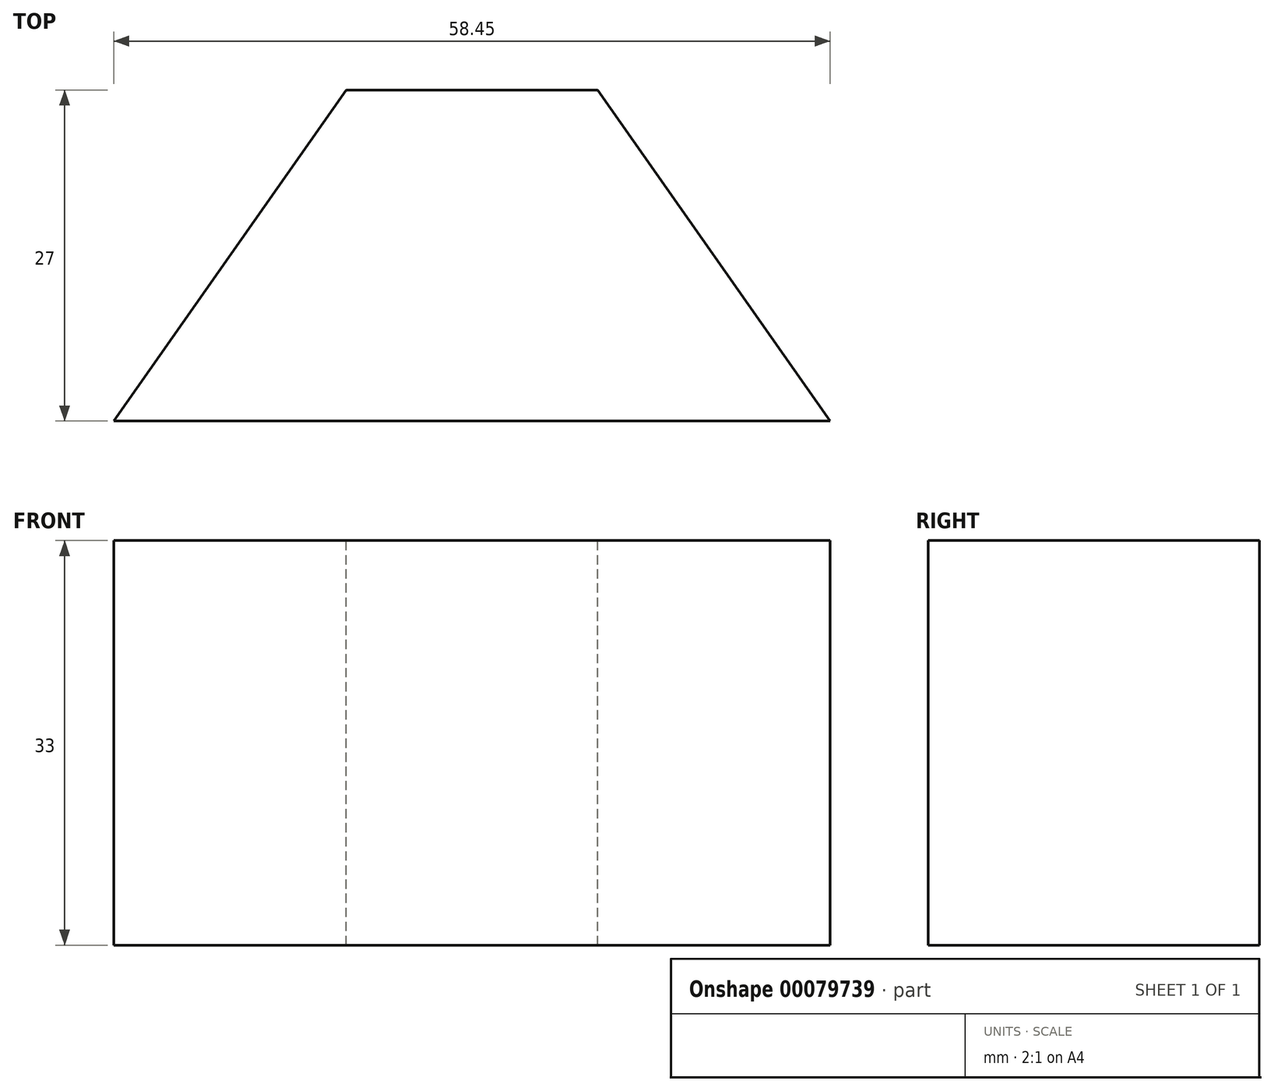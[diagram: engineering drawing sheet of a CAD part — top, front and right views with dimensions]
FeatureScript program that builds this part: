
annotation { "Feature Type Name" : "Feature", "Feature Type Description" : "" }
export const myFeature = defineFeature(function(context is Context, id is Id, definition is map)
    precondition{}
    {
        {
            var Q0;
            Q0=qCreatedBy(makeId("Front.planeOp"),FACE);
            var sketch = newSketch(context, id + "F0", { "sketchPlane" : qUnion([Q0])});
            skLineSegment(sketch, "E0.bottom", {"start": v(-28.62, 15.9) * mm, "end": v(29.83, 15.9) * mm});
            skLineSegment(sketch, "E0.top", {"start": v(-28.62, -17.1) * mm, "end": v(29.83, -17.1) * mm});
            skLineSegment(sketch, "E0.left", {"start": v(-28.62, 15.9) * mm, "end": v(-28.62, -17.1) * mm});
            skLineSegment(sketch, "E0.right", {"start": v(29.83, 15.9) * mm, "end": v(29.83, -17.1) * mm});
            skLineSegment(sketch, "E1.bottom", {"start": v(-4.12, -17.1) * mm, "end": v(8.88, -17.1) * mm});
            skLineSegment(sketch, "E1.top", {"start": v(-4.12, -8.35) * mm, "end": v(8.88, -8.35) * mm});
            skLineSegment(sketch, "E1.left", {"start": v(-4.12, -17.1) * mm, "end": v(-4.12, -8.35) * mm});
            skLineSegment(sketch, "E1.right", {"start": v(8.88, -17.1) * mm, "end": v(8.88, -8.35) * mm});
            skSolve(sketch);
        }
        {
            var Q0;
            Q0 = qSketchRegion(id + "F0", true);
            var Q1;
            Q1=makeQuery(id+"F0.imprint","IMPRINT",FACE,{"disambiguationData":[TD([[makeQuery(id+"F0.imprint","IMPRINT",EDGE,{"derivedFrom":sQuery(id+"F0.wireOp",EDGE,"E0.bottom")}),-1.0]])]});
            extrude(context, id + "F1", {"entities" : qUnion([Q0, Q1]), "depth" : 27 * mm});
        }
        {
            var Q0;
            Q0=makeQuery(id+"F1.opExtrude","SWEPT_FACE",FACE,{"disambiguationData":[OSD([sQuery(id+"F0.wireOp",EDGE,"E0.bottom")])]});
            var sketch = newSketch(context, id + "F2", { "sketchPlane" : qUnion([Q0])});
            skLineSegment(sketch, "E2", {"start": v(-28.62, -27) * mm, "end": v(-9.64, 0) * mm});
            skLineSegment(sketch, "E3", {"start": v(29.83, -27) * mm, "end": v(10.86, 0) * mm});
            skSolve(sketch);
        }
        {
            var Q0;
            Q0 = qSketchRegion(id + "F2", true);
            var Q1;
            {var subQ0=sQuery(id+"F2.wireOp",EDGE,"E2");Q1=makeQuery(id+"F2.imprint","IMPRINT",FACE,{"disambiguationData":[TD([[makeQuery(id+"F2.imprint","IMPRINT",EDGE,{"derivedFrom":subQ0}),1.0]])]});}
            var Q2;
            {var subQ0=sQuery(id+"F2.wireOp",EDGE,"E3");Q2=makeQuery(id+"F2.imprint","IMPRINT",FACE,{"disambiguationData":[TD([[makeQuery(id+"F2.imprint","IMPRINT",EDGE,{"derivedFrom":subQ0}),-1.0]])]});}
            extrude(context, id + "F3", {"entities" : qUnion([Q0, Q1, Q2]), "operationType" : NewBodyOperationType.REMOVE, "oppositeDirection" : true, "depth" : 33 * mm});
        }
    });
